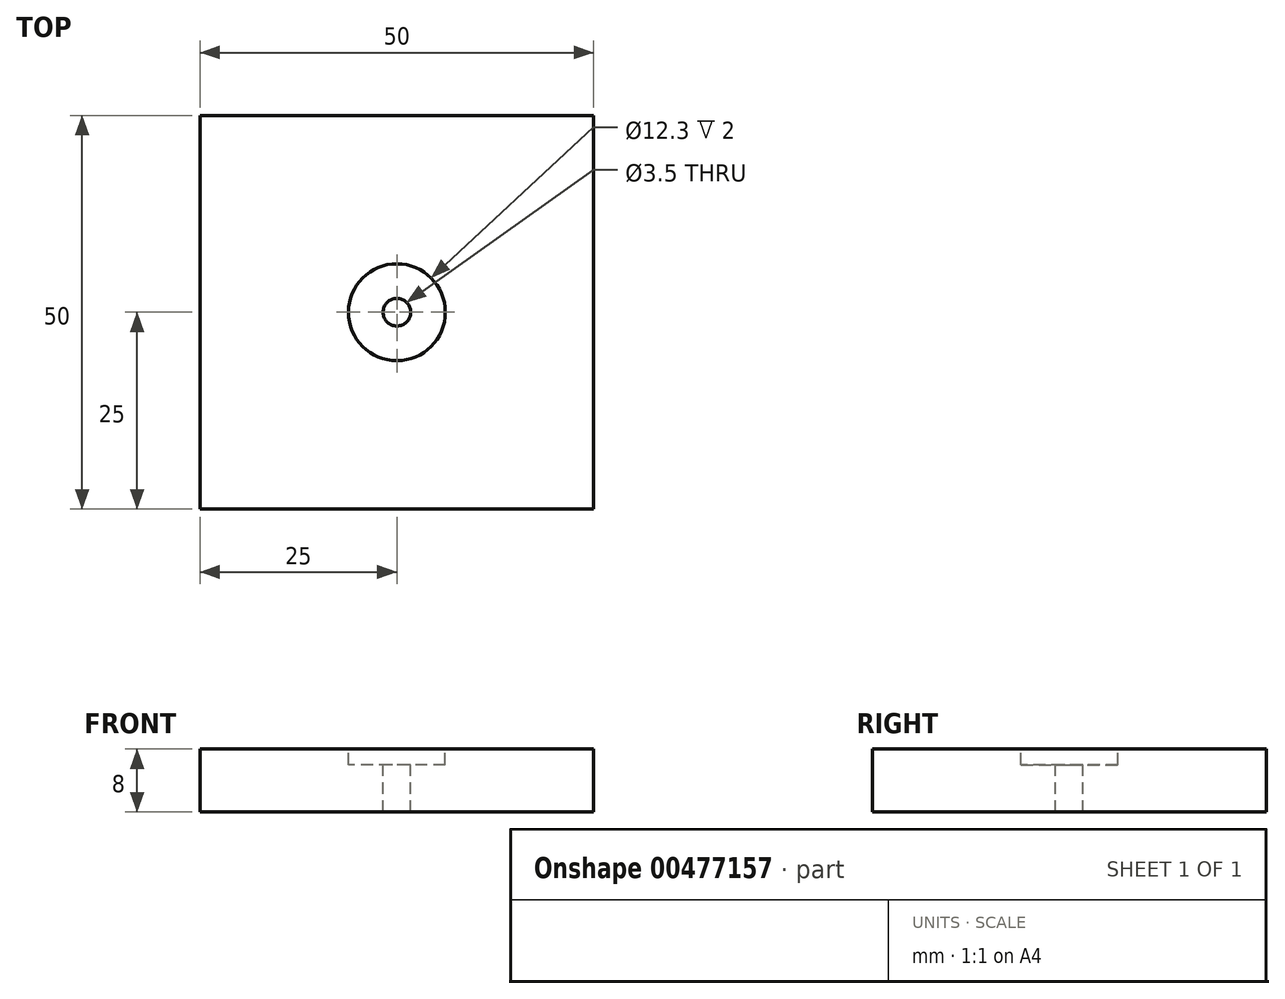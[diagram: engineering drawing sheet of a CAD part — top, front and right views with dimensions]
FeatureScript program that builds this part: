
annotation { "Feature Type Name" : "Feature", "Feature Type Description" : "" }
export const myFeature = defineFeature(function(context is Context, id is Id, definition is map)
    precondition{}
    {
        {
            var Q0;
            Q0=qCreatedBy(makeId("Top.planeOp"),FACE);
            var sketch = newSketch(context, id + "F0", { "sketchPlane" : qUnion([Q0])});
            skLineSegment(sketch, "E0.bottom", {"start": v(-25, 25) * mm, "end": v(25, 25) * mm});
            skLineSegment(sketch, "E0.top", {"start": v(-25, -25) * mm, "end": v(25, -25) * mm});
            skLineSegment(sketch, "E0.left", {"start": v(-25, 25) * mm, "end": v(-25, -25) * mm});
            skLineSegment(sketch, "E0.right", {"start": v(25, 25) * mm, "end": v(25, -25) * mm});
            skPoint(sketch, "E0.middle", {"position": v(0, 0) * mm});
            skSolve(sketch);
        }
        {
            var Q0;
            Q0=makeQuery(id+"F0.imprint","IMPRINT",FACE,{"disambiguationData":[TD([[makeQuery(id+"F0.imprint","IMPRINT",EDGE,{"derivedFrom":sQuery(id+"F0.wireOp",EDGE,"E0.bottom")}),-1.0]])]});
            extrude(context, id + "F1", {"entities" : qUnion([Q0]), "oppositeDirection" : true, "depth" : 8 * mm, "offsetDistance" : 25 * mm});
        }
        {
            var Q0;
            Q0=makeQuery(id+"F1.opExtrude","CAP_FACE",FACE,{"disambiguationData":[OSD([sQuery(id+"F0.wireOp",EDGE,"E0.bottom"),sQuery(id+"F0.wireOp",EDGE,"E0.top"),sQuery(id+"F0.wireOp",EDGE,"E0.left"),sQuery(id+"F0.wireOp",EDGE,"E0.right")])],"isStart":true});
            var sketch = newSketch(context, id + "F2", { "sketchPlane" : qUnion([Q0])});
            skCircle(sketch, "E1", {"center": v(0, 0) * mm, "radius": 6.15 * mm});
            skSolve(sketch);
        }
        {
            var Q0;
            Q0 = qSketchRegion(id + "F2", true);
            extrude(context, id + "F3", {"entities" : qUnion([Q0]), "operationType" : NewBodyOperationType.REMOVE, "oppositeDirection" : true, "depth" : 2 * mm, "offsetDistance" : 25 * mm});
        }
        {
            var Q0;
            Q0=makeQuery(id+"F3.boolean.opBoolean","COPY",FACE,{"derivedFrom":makeQuery(id+"F3.opExtrude","CAP_FACE",FACE,{"disambiguationData":[OSD([sQuery(id+"F2.wireOp",EDGE,"E1")])],"isStart":false})});
            var sketch = newSketch(context, id + "F4", { "sketchPlane" : qUnion([Q0])});
            skCircle(sketch, "E2", {"center": v(0, 0) * mm, "radius": 1.75 * mm});
            skSolve(sketch);
        }
        {
            var Q0;
            Q0 = qSketchRegion(id + "F4", true);
            extrude(context, id + "F5", {"entities" : qUnion([Q0]), "operationType" : NewBodyOperationType.REMOVE, "endBound" : BoundingType.THROUGH_ALL, "oppositeDirection" : true, "depth" : 25 * mm, "offsetDistance" : 25 * mm});
        }
    });
